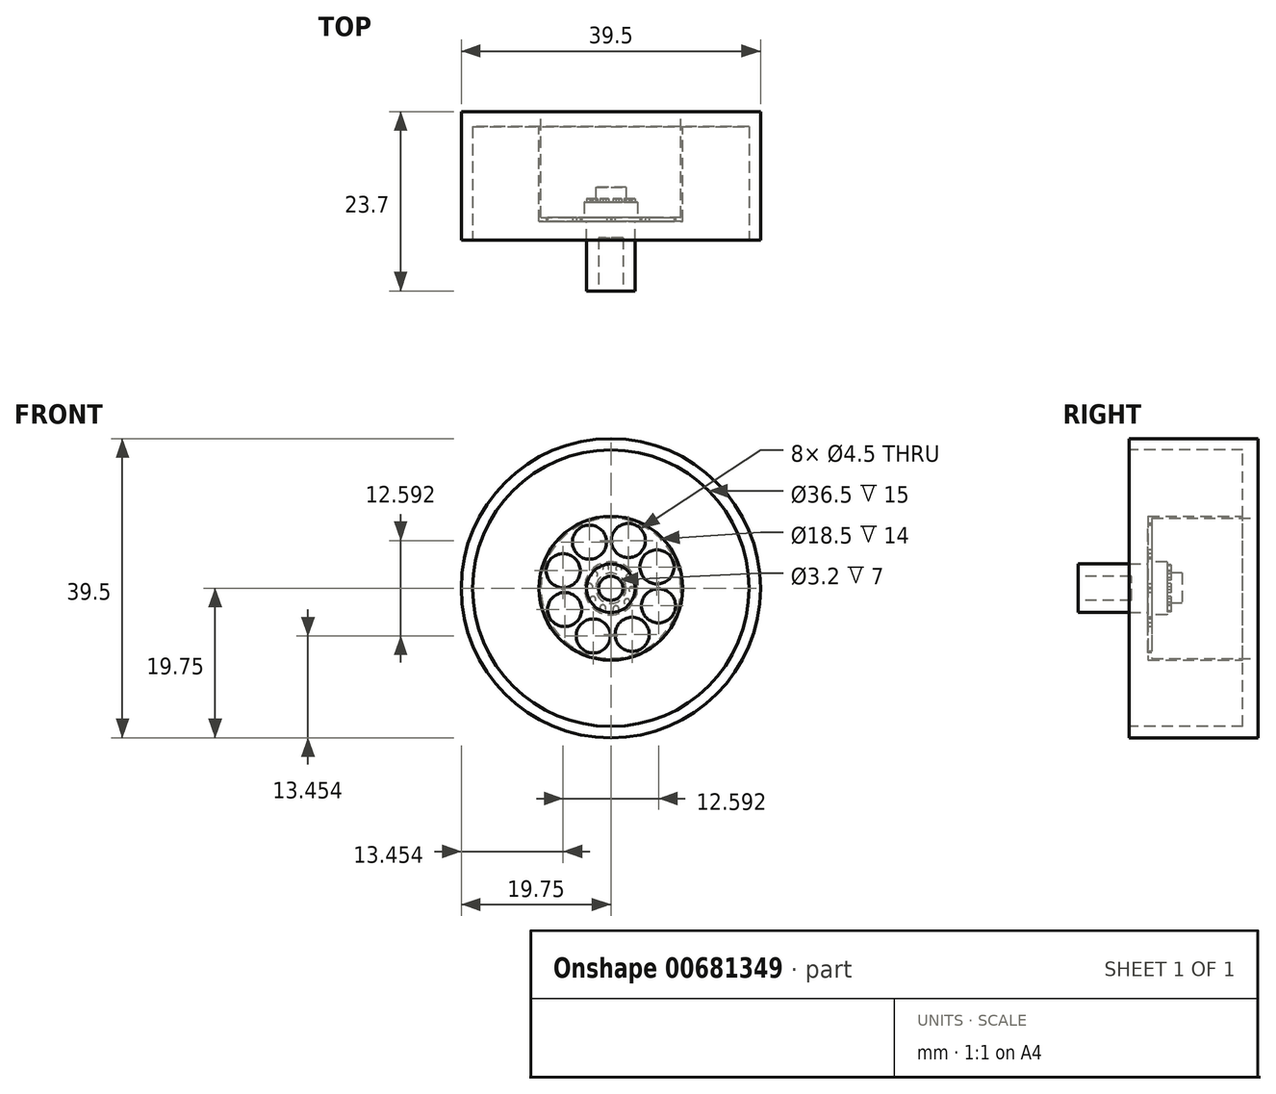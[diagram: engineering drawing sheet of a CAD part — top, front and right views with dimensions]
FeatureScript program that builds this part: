
annotation { "Feature Type Name" : "Feature", "Feature Type Description" : "" }
export const myFeature = defineFeature(function(context is Context, id is Id, definition is map)
    precondition{}
    {
        {
            var Q0;
            Q0=qCreatedBy(makeId("Front.planeOp"),FACE);
            var sketch = newSketch(context, id + "F0", { "sketchPlane" : qUnion([Q0])});
            skCircle(sketch, "E0", {"center": v(0, 0) * mm, "radius": 19.75 * mm});
            skSolve(sketch);
        }
        {
            var Q0;
            Q0 = qSketchRegion(id + "F0", true);
            extrude(context, id + "F1", {"entities" : qUnion([Q0]), "depth" : 17 * mm, "offsetDistance" : 25.4 * mm});
        }
        {
            var Q0;
            Q0=makeQuery(id+"F1.opExtrude","CAP_FACE",FACE,{"disambiguationData":[OSD([sQuery(id+"F0.wireOp",EDGE,"E0")])],"isStart":false});
            var sketch = newSketch(context, id + "F2", { "sketchPlane" : qUnion([Q0])});
            skCircle(sketch, "E1", {"center": v(0, 0) * mm, "radius": 18.25 * mm});
            skSolve(sketch);
        }
        {
            var Q0;
            Q0=makeQuery(id+"F2.imprint","IMPRINT",FACE,{"disambiguationData":[TD([[makeQuery(id+"F2.imprint","IMPRINT",EDGE,{"derivedFrom":sQuery(id+"F2.wireOp",EDGE,"E1")}),1.0]])]});
            extrude(context, id + "F3", {"entities" : qUnion([Q0]), "operationType" : NewBodyOperationType.REMOVE, "oppositeDirection" : true, "depth" : 15 * mm, "offsetDistance" : 25.4 * mm});
        }
        {
            var Q0;
            Q0=makeQuery(id+"F1.opExtrude","CAP_FACE",FACE,{"disambiguationData":[OSD([sQuery(id+"F0.wireOp",EDGE,"E0")])],"isStart":true});
            var sketch = newSketch(context, id + "F4", { "sketchPlane" : qUnion([Q0])});
            skCircle(sketch, "E2", {"center": v(0, 0) * mm, "radius": 9.5 * mm});
            skSolve(sketch);
        }
        {
            var Q0;
            Q0 = qSketchRegion(id + "F4", true);
            extrude(context, id + "F5", {"entities" : qUnion([Q0]), "operationType" : NewBodyOperationType.ADD, "oppositeDirection" : true, "depth" : 14.5 * mm, "offsetDistance" : 25.4 * mm});
        }
        {
            var Q0;
            Q0=makeQuery(id+"F1.opExtrude","CAP_FACE",FACE,{"disambiguationData":[OSD([sQuery(id+"F0.wireOp",EDGE,"E0")])],"isStart":true});
            var sketch = newSketch(context, id + "F6", { "sketchPlane" : qUnion([Q0])});
            skCircle(sketch, "E3", {"center": v(0, 0) * mm, "radius": 9.25 * mm});
            skSolve(sketch);
        }
        {
            var Q0;
            Q0 = qSketchRegion(id + "F6", true);
            extrude(context, id + "F7", {"entities" : qUnion([Q0]), "operationType" : NewBodyOperationType.REMOVE, "oppositeDirection" : true, "depth" : 14 * mm, "offsetDistance" : 25.4 * mm});
        }
        {
            var Q0;
            Q0=makeQuery(id+"F5.opExtrude","CAP_FACE",FACE,{"disambiguationData":[OSD([sQuery(id+"F4.wireOp",EDGE,"E2")])],"isStart":false});
            var sketch = newSketch(context, id + "F8", { "sketchPlane" : qUnion([Q0])});
            skCircle(sketch, "E4", {"center": v(0, 0) * mm, "radius": 3.2 * mm});
            skSolve(sketch);
        }
        {
            var Q0;
            Q0 = qSketchRegion(id + "F8", true);
            extrude(context, id + "F9", {"entities" : qUnion([Q0]), "operationType" : NewBodyOperationType.ADD, "depth" : 9.2 * mm, "offsetDistance" : 25.4 * mm});
        }
        {
            var Q0;
            Q0=makeQuery(id+"F9.opExtrude","CAP_FACE",FACE,{"disambiguationData":[OSD([sQuery(id+"F8.wireOp",EDGE,"E4")])],"isStart":false});
            var sketch = newSketch(context, id + "F10", { "sketchPlane" : qUnion([Q0])});
            skCircle(sketch, "E5", {"center": v(0, 0) * mm, "radius": 1.6 * mm});
            skSolve(sketch);
        }
        {
            var Q0;
            Q0 = qSketchRegion(id + "F10", true);
            extrude(context, id + "F11", {"entities" : qUnion([Q0]), "operationType" : NewBodyOperationType.REMOVE, "oppositeDirection" : true, "depth" : 7 * mm, "offsetDistance" : 25.4 * mm});
        }
        {
            var Q0;
            Q0=makeQuery(id+"F5.opExtrude","CAP_FACE",FACE,{"disambiguationData":[OSD([sQuery(id+"F4.wireOp",EDGE,"E2")])],"isStart":false});
            var sketch = newSketch(context, id + "F12", { "sketchPlane" : qUnion([Q0])});
            skCircle(sketch, "E6", {"center": v(2.32, 6.3) * mm, "radius": 2.25 * mm});
            skCircle(sketch, "E7.1.0", {"center": v(-2.81, 6.1) * mm, "radius": 2.25 * mm});
            skCircle(sketch, "E7.2.0", {"center": v(-6.3, 2.32) * mm, "radius": 2.25 * mm});
            skCircle(sketch, "E7.3.0", {"center": v(-6.1, -2.81) * mm, "radius": 2.25 * mm});
            skCircle(sketch, "E7.4.0", {"center": v(-2.32, -6.3) * mm, "radius": 2.25 * mm});
            skCircle(sketch, "E7.5.0", {"center": v(2.81, -6.1) * mm, "radius": 2.25 * mm});
            skCircle(sketch, "E7.6.0", {"center": v(6.3, -2.32) * mm, "radius": 2.25 * mm});
            skCircle(sketch, "E7.7.0", {"center": v(6.1, 2.81) * mm, "radius": 2.25 * mm});
            skPoint(sketch, "E7.center", {"position": v(0, 0) * mm});
            skSolve(sketch);
        }
        {
            var Q0;
            Q0=makeQuery(id+"F12.imprint","IMPRINT",FACE,{"disambiguationData":[TD([[makeQuery(id+"F12.imprint","IMPRINT",EDGE,{"derivedFrom":sQuery(id+"F12.wireOp",EDGE,"E7.1.0")}),1.0]])]});
            var Q1;
            Q1=makeQuery(id+"F12.imprint","IMPRINT",FACE,{"disambiguationData":[TD([[makeQuery(id+"F12.imprint","IMPRINT",EDGE,{"derivedFrom":sQuery(id+"F12.wireOp",EDGE,"E6")}),1.0]])]});
            var Q2;
            Q2=makeQuery(id+"F12.imprint","IMPRINT",FACE,{"disambiguationData":[TD([[makeQuery(id+"F12.imprint","IMPRINT",EDGE,{"derivedFrom":sQuery(id+"F12.wireOp",EDGE,"E7.7.0")}),1.0]])]});
            var Q3;
            Q3=makeQuery(id+"F12.imprint","IMPRINT",FACE,{"disambiguationData":[TD([[makeQuery(id+"F12.imprint","IMPRINT",EDGE,{"derivedFrom":sQuery(id+"F12.wireOp",EDGE,"E7.6.0")}),1.0]])]});
            var Q4;
            Q4=makeQuery(id+"F12.imprint","IMPRINT",FACE,{"disambiguationData":[TD([[makeQuery(id+"F12.imprint","IMPRINT",EDGE,{"derivedFrom":sQuery(id+"F12.wireOp",EDGE,"E7.5.0")}),1.0]])]});
            var Q5;
            Q5=makeQuery(id+"F12.imprint","IMPRINT",FACE,{"disambiguationData":[TD([[makeQuery(id+"F12.imprint","IMPRINT",EDGE,{"derivedFrom":sQuery(id+"F12.wireOp",EDGE,"E7.4.0")}),1.0]])]});
            var Q6;
            Q6=makeQuery(id+"F12.imprint","IMPRINT",FACE,{"disambiguationData":[TD([[makeQuery(id+"F12.imprint","IMPRINT",EDGE,{"derivedFrom":sQuery(id+"F12.wireOp",EDGE,"E7.3.0")}),1.0]])]});
            var Q7;
            Q7=makeQuery(id+"F12.imprint","IMPRINT",FACE,{"disambiguationData":[TD([[makeQuery(id+"F12.imprint","IMPRINT",EDGE,{"derivedFrom":sQuery(id+"F12.wireOp",EDGE,"E7.2.0")}),1.0]])]});
            extrude(context, id + "F13", {"entities" : qUnion([Q0, Q1, Q2, Q3, Q4, Q5, Q6, Q7]), "operationType" : NewBodyOperationType.REMOVE, "oppositeDirection" : true, "depth" : 25.4 * mm, "offsetDistance" : 25.4 * mm});
        }
        {
            var Q0;
            Q0=makeQuery(id+"F7.boolean.opBoolean","COPY",FACE,{"derivedFrom":makeQuery(id+"F7.opExtrude","CAP_FACE",FACE,{"disambiguationData":[OSD([sQuery(id+"F6.wireOp",EDGE,"E3")])],"isStart":false})});
            var sketch = newSketch(context, id + "F14", { "sketchPlane" : qUnion([Q0])});
            skCircle(sketch, "E8", {"center": v(0, 0) * mm, "radius": 3.5 * mm});
            skSolve(sketch);
        }
        {
            var Q0;
            Q0 = qSketchRegion(id + "F14", true);
            extrude(context, id + "F15", {"entities" : qUnion([Q0]), "operationType" : NewBodyOperationType.ADD, "depth" : 2 * mm, "offsetDistance" : 25.4 * mm});
        }
        {
            var Q0;
            Q0=makeQuery(id+"F15.opExtrude","CAP_FACE",FACE,{"disambiguationData":[OSD([sQuery(id+"F14.wireOp",EDGE,"E8")])],"isStart":false});
            var sketch = newSketch(context, id + "F16", { "sketchPlane" : qUnion([Q0])});
            skCircle(sketch, "E9", {"center": v(0, 0) * mm, "radius": 2 * mm});
            skSolve(sketch);
        }
        {
            var Q0;
            Q0 = qSketchRegion(id + "F16", true);
            extrude(context, id + "F17", {"entities" : qUnion([Q0]), "operationType" : NewBodyOperationType.ADD, "depth" : 2 * mm, "offsetDistance" : 25.4 * mm});
        }
        {
            var Q0;
            Q0=makeQuery(id+"F15.opExtrude","CAP_FACE",FACE,{"disambiguationData":[OSD([sQuery(id+"F14.wireOp",EDGE,"E8")])],"isStart":false});
            var sketch = newSketch(context, id + "F18", { "sketchPlane" : qUnion([Q0])});
            skCircle(sketch, "E10", {"center": v(-1.05, 2.6) * mm, "radius": 0.4 * mm});
            skCircle(sketch, "E11.1.0", {"center": v(-2.38, 1.48) * mm, "radius": 0.4 * mm});
            skCircle(sketch, "E11.2.0", {"center": v(-2.8, -0.2) * mm, "radius": 0.4 * mm});
            skCircle(sketch, "E11.3.0", {"center": v(-2.14, -1.8) * mm, "radius": 0.4 * mm});
            skCircle(sketch, "E11.4.0", {"center": v(-0.67, -2.72) * mm, "radius": 0.4 * mm});
            skCircle(sketch, "E11.5.0", {"center": v(1.05, -2.6) * mm, "radius": 0.4 * mm});
            skCircle(sketch, "E11.6.0", {"center": v(2.38, -1.48) * mm, "radius": 0.4 * mm});
            skCircle(sketch, "E11.7.0", {"center": v(2.8, 0.2) * mm, "radius": 0.4 * mm});
            skCircle(sketch, "E11.8.0", {"center": v(2.14, 1.8) * mm, "radius": 0.4 * mm});
            skCircle(sketch, "E11.9.0", {"center": v(0.67, 2.72) * mm, "radius": 0.4 * mm});
            skPoint(sketch, "E11.center", {"position": v(0, 0) * mm});
            skSolve(sketch);
        }
        {
            var Q0;
            Q0=makeQuery(id+"F18.imprint","IMPRINT",FACE,{"disambiguationData":[TD([[makeQuery(id+"F18.imprint","IMPRINT",EDGE,{"derivedFrom":sQuery(id+"F18.wireOp",EDGE,"E11.3.0")}),1.0]])]});
            var Q1;
            Q1=makeQuery(id+"F18.imprint","IMPRINT",FACE,{"disambiguationData":[TD([[makeQuery(id+"F18.imprint","IMPRINT",EDGE,{"derivedFrom":sQuery(id+"F18.wireOp",EDGE,"E11.4.0")}),1.0]])]});
            var Q2;
            Q2=makeQuery(id+"F18.imprint","IMPRINT",FACE,{"disambiguationData":[TD([[makeQuery(id+"F18.imprint","IMPRINT",EDGE,{"derivedFrom":sQuery(id+"F18.wireOp",EDGE,"E11.5.0")}),1.0]])]});
            var Q3;
            Q3=makeQuery(id+"F18.imprint","IMPRINT",FACE,{"disambiguationData":[TD([[makeQuery(id+"F18.imprint","IMPRINT",EDGE,{"derivedFrom":sQuery(id+"F18.wireOp",EDGE,"E11.6.0")}),1.0]])]});
            var Q4;
            Q4=makeQuery(id+"F18.imprint","IMPRINT",FACE,{"disambiguationData":[TD([[makeQuery(id+"F18.imprint","IMPRINT",EDGE,{"derivedFrom":sQuery(id+"F18.wireOp",EDGE,"E11.7.0")}),1.0]])]});
            var Q5;
            Q5=makeQuery(id+"F18.imprint","IMPRINT",FACE,{"disambiguationData":[TD([[makeQuery(id+"F18.imprint","IMPRINT",EDGE,{"derivedFrom":sQuery(id+"F18.wireOp",EDGE,"E11.8.0")}),1.0]])]});
            var Q6;
            Q6=makeQuery(id+"F18.imprint","IMPRINT",FACE,{"disambiguationData":[TD([[makeQuery(id+"F18.imprint","IMPRINT",EDGE,{"derivedFrom":sQuery(id+"F18.wireOp",EDGE,"E11.9.0")}),1.0]])]});
            var Q7;
            Q7=makeQuery(id+"F18.imprint","IMPRINT",FACE,{"disambiguationData":[TD([[makeQuery(id+"F18.imprint","IMPRINT",EDGE,{"derivedFrom":sQuery(id+"F18.wireOp",EDGE,"E10")}),1.0]])]});
            var Q8;
            Q8=makeQuery(id+"F18.imprint","IMPRINT",FACE,{"disambiguationData":[TD([[makeQuery(id+"F18.imprint","IMPRINT",EDGE,{"derivedFrom":sQuery(id+"F18.wireOp",EDGE,"E11.2.0")}),1.0]])]});
            var Q9;
            Q9=makeQuery(id+"F18.imprint","IMPRINT",FACE,{"disambiguationData":[TD([[makeQuery(id+"F18.imprint","IMPRINT",EDGE,{"derivedFrom":sQuery(id+"F18.wireOp",EDGE,"E11.1.0")}),1.0]])]});
            extrude(context, id + "F19", {"entities" : qUnion([Q0, Q1, Q2, Q3, Q4, Q5, Q6, Q7, Q8, Q9]), "operationType" : NewBodyOperationType.ADD, "depth" : .5 * mm, "offsetDistance" : 25.4 * mm});
        }
    });
